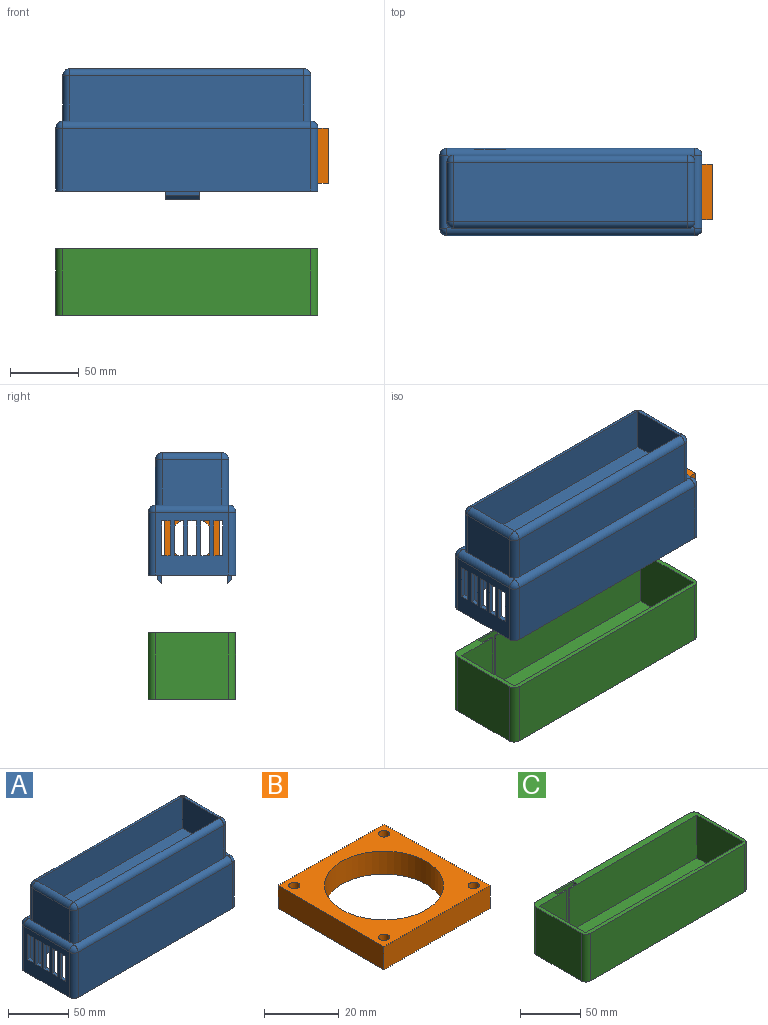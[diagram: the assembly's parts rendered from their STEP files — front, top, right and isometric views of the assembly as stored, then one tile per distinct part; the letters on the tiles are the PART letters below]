
ASSEMBLY  parts=3 mates=2
PART A: 101 faces, bbox 190.5x63.5x95.3 mm
  f0: plane 190.5x63.5mm, normal (0,0,-1), area 2015.9mm2, adj f1,f2,f3,f4,f5,f6,f7,f8
  f1: plane 184.15x47.63mm, normal (0,1,0), area 8657.2mm2, adj f0,f4,f5,f14,f68,f69,f71
  f2: plane 53.34x45.72mm, normal (-1,0,0), area 1632.3mm2, adj f0,f10,f11,f23,f48,f49,f50,f51
  f3: plane 53.34x45.72mm, normal (1,0,0), area 1632.3mm2, adj f0,f9,f12,f24,f28,f29,f30,f31
  f4: plane 53.98x47.63mm, normal (1,0,0), area 1764.1mm2, adj f0,f1,f6,f14,f48,f49,f50,f51
  f5: plane 53.98x47.63mm, normal (-1,0,0), area 1764.1mm2, adj f0,f1,f13,f14,f28,f29,f30,f31
  f6: plane 47.63x22.23mm, normal (0,-1,0), area 1058.5mm2, adj f0,f4,f14,f16
  f7: plane 180.34x45.72mm, normal (0,1,0), area 8245.1mm2, adj f0,f11,f12,f27
  f8: plane 180.34x45.72mm, normal (0,-1,0), area 8245.1mm2, adj f0,f9,f10,f20
  f9: cylinder r=5.08mm len=45.72mm, axis (0,0,1), area 364.8mm2, adj f0,f3,f8,f22
  f10: cylinder r=5.08mm len=45.72mm, axis (0,0,-1), area 364.8mm2, adj f0,f2,f8,f21
  f11: cylinder r=5.08mm len=45.72mm, axis (0,0,1), area 364.8mm2, adj f0,f2,f7,f25
  f12: cylinder r=5.08mm len=45.72mm, axis (0,0,-1), area 364.8mm2, adj f0,f3,f7,f26
  f13: plane 139.57x47.63mm, normal (0,-1,0), area 6534.3mm2, adj f0,f5,f14,f18,f74,f75,f77
  f14: plane 184.15x53.98mm, normal (0,0,-1), area 9939.5mm2, adj f1,f4,f5,f6,f13,f15
  f15: plane 22.35x0.64mm, normal (0,1,0), area 14.2mm2, adj f14,f16,f18,f19
  f16: plane 48.26x5.33mm, normal (1,0,0), area 257.4mm2, adj f0,f6,f15,f17,f19
  f17: plane 48.26x22.35mm, normal (0,-1,0), area 1078.7mm2, adj f0,f16,f18,f19
  f18: plane 48.26x5.33mm, normal (-1,0,0), area 257.4mm2, adj f0,f13,f15,f17,f19
  f19: plane 22.35x5.33mm, normal (0,0,-1), area 119.2mm2, adj f15,f16,f17,f18
  f20: cylinder r=5.08mm len=180.34mm, axis (-1,0,0), area 1444.6mm2, adj f8,f21,f22,f23,f24,f83,f87,f95
  f21: sphere r=5.08mm, area 40.5mm2, adj f10,f20,f23
  f22: sphere r=5.08mm, area 40.5mm2, adj f9,f20,f24
  f23: cylinder r=5.08mm len=53.34mm, axis (0,1,0), area 431.2mm2, adj f2,f20,f21,f25,f27,f82,f87,f90
  f24: cylinder r=5.08mm len=53.34mm, axis (0,-1,0), area 431.2mm2, adj f3,f20,f22,f26,f27,f80,f91,f95
  f25: sphere r=5.08mm, area 40.5mm2, adj f11,f23,f27
  f26: sphere r=5.08mm, area 40.5mm2, adj f12,f24,f27
  f27: cylinder r=5.08mm len=180.34mm, axis (1,0,0), area 1444.6mm2, adj f7,f23,f24,f25,f26,f81,f90,f91
  f28: plane 25.4x3.18mm, normal (0,-1,0), area 80.6mm2, adj f3,f5,f29,f31
  f29: plane 6.35x3.18mm, normal (0,0,1), area 20.2mm2, adj f3,f5,f28,f30
  f30: plane 25.4x3.18mm, normal (0,1,0), area 80.6mm2, adj f3,f5,f29,f31
  f31: plane 6.35x3.18mm, normal (0,0,-1), area 20.2mm2, adj f3,f5,f28,f30
  f32: plane 25.4x3.18mm, normal (0,-1,0), area 80.6mm2, adj f3,f5,f33,f35
  f33: plane 6.35x3.18mm, normal (0,0,1), area 20.2mm2, adj f3,f5,f32,f34
  f34: plane 25.4x3.18mm, normal (0,1,0), area 80.6mm2, adj f3,f5,f33,f35
  f35: plane 6.35x3.18mm, normal (0,0,-1), area 20.2mm2, adj f3,f5,f32,f34
  f36: plane 25.4x3.18mm, normal (0,-1,0), area 80.6mm2, adj f3,f5,f37,f39
  f37: plane 6.35x3.18mm, normal (0,0,1), area 20.2mm2, adj f3,f5,f36,f38
  f38: plane 25.4x3.18mm, normal (0,1,0), area 80.6mm2, adj f3,f5,f37,f39
  f39: plane 6.35x3.18mm, normal (0,0,-1), area 20.2mm2, adj f3,f5,f36,f38
  f40: plane 25.4x3.18mm, normal (0,-1,0), area 80.6mm2, adj f3,f5,f41,f43
  f41: plane 6.35x3.18mm, normal (0,0,1), area 20.2mm2, adj f3,f5,f40,f42
  f42: plane 25.4x3.18mm, normal (0,1,0), area 80.6mm2, adj f3,f5,f41,f43
  f43: plane 6.35x3.18mm, normal (0,0,-1), area 20.2mm2, adj f3,f5,f40,f42
  f44: plane 25.4x3.18mm, normal (0,-1,0), area 80.6mm2, adj f3,f5,f45,f47
  f45: plane 6.35x3.18mm, normal (0,0,1), area 20.2mm2, adj f3,f5,f44,f46
  f46: plane 25.4x3.18mm, normal (0,1,0), area 80.6mm2, adj f3,f5,f45,f47
  f47: plane 6.35x3.18mm, normal (0,0,-1), area 20.2mm2, adj f3,f5,f44,f46
  f48: plane 6.35x3.18mm, normal (0,0,-1), area 20.2mm2, adj f2,f4,f49,f51
  f49: plane 25.4x3.18mm, normal (0,1,0), area 80.6mm2, adj f2,f4,f48,f50
  f50: plane 6.35x3.18mm, normal (0,0,1), area 20.2mm2, adj f2,f4,f49,f51
  f51: plane 25.4x3.18mm, normal (0,-1,0), area 80.6mm2, adj f2,f4,f48,f50
  f52: plane 6.35x3.18mm, normal (0,0,-1), area 20.2mm2, adj f2,f4,f53,f55
  f53: plane 25.4x3.18mm, normal (0,1,0), area 80.6mm2, adj f2,f4,f52,f54
  f54: plane 6.35x3.18mm, normal (0,0,1), area 20.2mm2, adj f2,f4,f53,f55
  f55: plane 25.4x3.18mm, normal (0,-1,0), area 80.6mm2, adj f2,f4,f52,f54
  f56: plane 6.35x3.18mm, normal (0,0,-1), area 20.2mm2, adj f2,f4,f57,f59
  f57: plane 25.4x3.18mm, normal (0,1,0), area 80.6mm2, adj f2,f4,f56,f58
  f58: plane 6.35x3.18mm, normal (0,0,1), area 20.2mm2, adj f2,f4,f57,f59
  f59: plane 25.4x3.18mm, normal (0,-1,0), area 80.6mm2, adj f2,f4,f56,f58
  f60: plane 6.35x3.18mm, normal (0,0,-1), area 20.2mm2, adj f2,f4,f61,f63
  f61: plane 25.4x3.18mm, normal (0,1,0), area 80.6mm2, adj f2,f4,f60,f62
  f62: plane 6.35x3.18mm, normal (0,0,1), area 20.2mm2, adj f2,f4,f61,f63
  f63: plane 25.4x3.18mm, normal (0,-1,0), area 80.6mm2, adj f2,f4,f60,f62
  f64: plane 6.35x3.18mm, normal (0,0,-1), area 20.2mm2, adj f2,f4,f65,f67
  f65: plane 25.4x3.18mm, normal (0,1,0), area 80.6mm2, adj f2,f4,f64,f66
  f66: plane 6.35x3.18mm, normal (0,0,1), area 20.2mm2, adj f2,f4,f65,f67
  f67: plane 25.4x3.18mm, normal (0,-1,0), area 80.6mm2, adj f2,f4,f64,f66
  f68: plane 10.8x3.18mm, normal (-1,0,0), area 24.2mm2, adj f1,f70,f71,f72,f73
  f69: plane 10.8x3.18mm, normal (1,0,0), area 24.2mm2, adj f1,f70,f71,f72,f73
  f70: plane 25.4x7.62mm, normal (0,1,0), area 193.5mm2, adj f68,f69,f71,f73
  f71: plane 25.4x3.18mm, normal (0,0.71,0.71), area 114mm2, adj f1,f68,f69,f70
  f72: plane 25.4x3.18mm, normal (0,-1,0), area 80.6mm2, adj f0,f68,f69,f73
  f73: plane 25.4x3.18mm, normal (0,-0.71,-0.71), area 114mm2, adj f68,f69,f70,f72
  f74: plane 10.8x3.18mm, normal (1,0,0), area 24.2mm2, adj f13,f76,f77,f78,f79
  f75: plane 10.8x3.18mm, normal (-1,0,0), area 24.2mm2, adj f13,f76,f77,f78,f79
  f76: plane 25.4x7.62mm, normal (0,-1,0), area 193.5mm2, adj f74,f75,f77,f79
  f77: plane 25.4x3.18mm, normal (0,-0.71,0.71), area 114mm2, adj f13,f74,f75,f76
  f78: plane 25.4x3.18mm, normal (0,1,0), area 80.6mm2, adj f0,f74,f75,f79
  f79: plane 25.4x3.18mm, normal (0,0.71,-0.71), area 114mm2, adj f74,f75,f76,f78
  f80: plane 43.18x33.02mm, normal (1,0,0), area 1425.8mm2, adj f24,f91,f93,f95
  f81: plane 170.18x33.02mm, normal (0,1,0), area 5619.3mm2, adj f27,f88,f90,f91
  f82: plane 43.18x33.02mm, normal (-1,0,0), area 1425.8mm2, adj f23,f85,f87,f90
  f83: plane 170.18x33.02mm, normal (0,-1,0), area 5619.3mm2, adj f20,f84,f87,f95
  f84: cylinder r=5.08mm len=170.18mm, axis (-1,0,0), area 1358mm2, adj f83,f86,f94,f96
  f85: cylinder r=5.08mm len=43.18mm, axis (0,1,0), area 344.6mm2, adj f82,f86,f89,f99
  f86: sphere r=5.08mm, area 40.5mm2, adj f84,f85,f87
  f87: cylinder r=5.08mm len=33.24mm, axis (0,0,-1), area 263.9mm2, adj f20,f23,f82,f83,f86
  f88: cylinder r=5.08mm len=170.18mm, axis (1,0,0), area 1358mm2, adj f81,f89,f92,f98
  f89: sphere r=5.08mm, area 40.5mm2, adj f85,f88,f90
  f90: cylinder r=5.08mm len=33.24mm, axis (0,0,-1), area 263.9mm2, adj f23,f27,f81,f82,f89
  f91: cylinder r=5.08mm len=33.24mm, axis (0,0,-1), area 263.9mm2, adj f24,f27,f80,f81,f92
  f92: sphere r=5.08mm, area 40.5mm2, adj f88,f91,f93
  f93: cylinder r=5.08mm len=43.18mm, axis (0,-1,0), area 344.6mm2, adj f80,f92,f94,f97
  f94: sphere r=5.08mm, area 40.5mm2, adj f84,f93,f95
  f95: cylinder r=5.08mm len=33.24mm, axis (0,0,-1), area 263.9mm2, adj f20,f24,f80,f83,f94
  f96: plane 170.18x31.75mm, normal (0,1,0), area 5403.2mm2, adj f84,f97,f99,f100
  f97: plane 43.18x31.75mm, normal (-1,0,0), area 1371mm2, adj f93,f96,f98,f100
  f98: plane 170.18x31.75mm, normal (0,-1,0), area 5403.2mm2, adj f88,f97,f99,f100
  f99: plane 43.18x31.75mm, normal (1,0,0), area 1371mm2, adj f85,f96,f98,f100
  f100: plane 170.18x43.18mm, normal (0,0,1), area 7348.4mm2, adj f96,f97,f98,f99
PART B: 11 faces, bbox 40x40x7.5 mm
  f0: plane 40x7.5mm, normal (0,1,0), area 300mm2, adj f1,f3,f4,f5
  f1: plane 40x7.5mm, normal (-1,0,0), area 300mm2, adj f0,f2,f4,f5
  f2: plane 40x7.5mm, normal (0,-1,0), area 300mm2, adj f1,f3,f4,f5
  f3: plane 40x7.5mm, normal (1,0,0), area 300mm2, adj f0,f2,f4,f5
  f4: plane 40x40mm, normal (0,0,1), area 780mm2, adj f0,f1,f2,f3,f6,f7,f8,f9
  f5: plane 40x40mm, normal (0,0,-1), area 780mm2, adj f0,f1,f2,f3,f6,f7,f8,f9
  f6: cylinder r=15.88mm len=31.75mm, axis (0,0,1), area 748.1mm2, adj f4,f5
  f7: cylinder r=1.5mm len=7.5mm, axis (0,0,1), area 70.7mm2, adj f4,f5
  f8: cylinder r=1.5mm len=7.5mm, axis (0,0,1), area 70.7mm2, adj f4,f5
  f9: cylinder r=1.5mm len=7.5mm, axis (0,0,1), area 70.7mm2, adj f4,f5
  f10: cylinder r=1.5mm len=7.5mm, axis (0,0,1), area 70.7mm2, adj f4,f5
PART C: 23 faces, bbox 190.5x63.5x48.3 mm
  f0: plane 190.5x63.5mm, normal (0,0,1), area 2043.1mm2, adj f1,f2,f3,f4,f5,f7,f8,f9
  f1: plane 43.43x31.81mm, normal (0,-1,0), area 1381.8mm2, adj f0,f8,f11,f12
  f2: plane 180.34x48.26mm, normal (0,1,0), area 8703.2mm2, adj f0,f6,f20,f22
  f3: plane 53.34x48.26mm, normal (-1,0,0), area 2574.2mm2, adj f0,f6,f19,f20
  f4: plane 180.34x48.26mm, normal (0,-1,0), area 8703.2mm2, adj f0,f6,f19,f21
  f5: plane 53.34x48.26mm, normal (1,0,0), area 2574.2mm2, adj f0,f6,f21,f22
  f6: plane 190.5x63.5mm, normal (0,0,-1), area 12074.6mm2, adj f2,f3,f4,f5,f19,f20,f21,f22
  f7: plane 149.16x43.43mm, normal (0,-1,0), area 6478.7mm2, adj f0,f10,f11,f13
  f8: plane 53.98x43.43mm, normal (1,0,0), area 2344.4mm2, adj f0,f1,f9,f11
  f9: plane 184.15x43.43mm, normal (0,1,0), area 7998.4mm2, adj f0,f8,f10,f11
  f10: plane 53.98x43.43mm, normal (-1,0,0), area 2344.4mm2, adj f0,f7,f9,f11
  f11: plane 184.15x59.18mm, normal (0,0,1), area 10031.5mm2, adj f1,f7,f8,f9,f10,f12,f13,f14
  f12: plane 43.43x1.27mm, normal (1,0,0), area 55.2mm2, adj f0,f1,f11,f18
  f13: plane 43.43x1.27mm, normal (-1,0,0), area 55.2mm2, adj f0,f7,f11,f14
  f14: plane 43.43x9.59mm, normal (0,1,0), area 416.5mm2, adj f0,f11,f13,f15
  f15: plane 43.43x3.94mm, normal (-1,0,0), area 171mm2, adj f0,f11,f14,f16
  f16: plane 43.43x22.35mm, normal (0,-1,0), area 970.8mm2, adj f0,f11,f15,f17
  f17: plane 43.43x3.94mm, normal (1,0,0), area 171mm2, adj f0,f11,f16,f18
  f18: plane 43.43x9.59mm, normal (0,1,0), area 416.5mm2, adj f0,f11,f12,f17
  f19: cylinder r=5.08mm len=48.26mm, axis (0,0,-1), area 385.1mm2, adj f0,f3,f4,f6
  f20: cylinder r=5.08mm len=48.26mm, axis (0,0,1), area 385.1mm2, adj f0,f2,f3,f6
  f21: cylinder r=5.08mm len=48.26mm, axis (0,0,1), area 385.1mm2, adj f0,f4,f5,f6
  f22: cylinder r=5.08mm len=48.26mm, axis (0,0,-1), area 385.1mm2, adj f0,f2,f5,f6
PLACE A t=(-11.81,-13.46,90.33)mm
PLACE B rot(axis=(0,-1,0),90deg) t=(94.36,-22.24,163.73)mm
PLACE C at identity fixed
MATE fastened A.f3 <-> B.f4  axis (1,0,0) through (86.86,-42.24,136.05)mm
MATE slider C.f0 <-> A.f0  axis (0,0,1) through (-78.24,-11.5,48.26)mm
